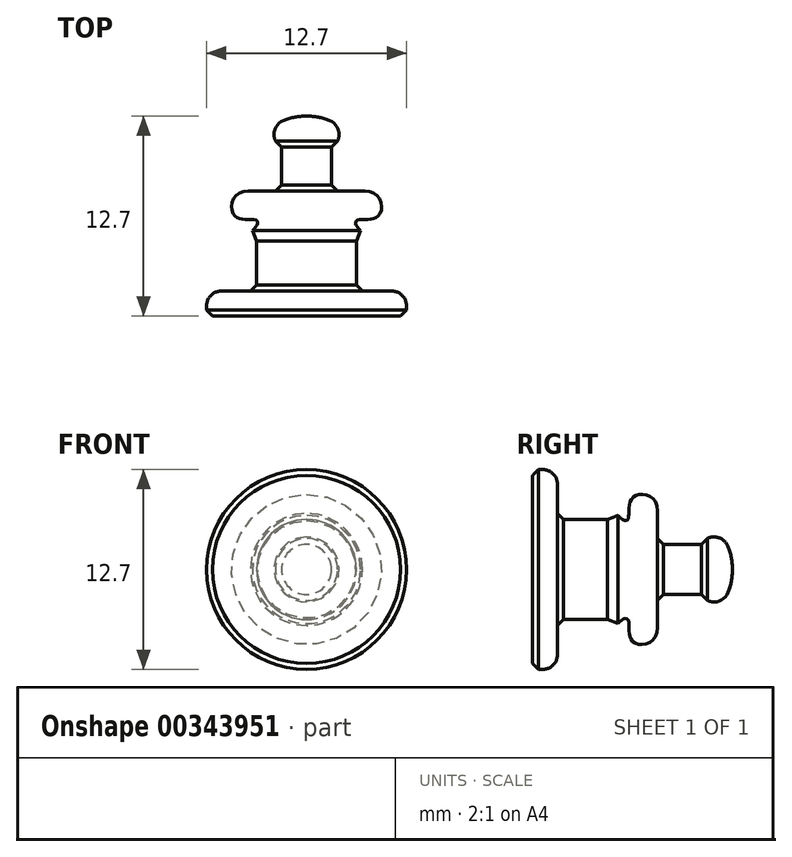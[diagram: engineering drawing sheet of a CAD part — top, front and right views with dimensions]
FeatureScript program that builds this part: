
annotation { "Feature Type Name" : "Feature", "Feature Type Description" : "" }
export const myFeature = defineFeature(function(context is Context, id is Id, definition is map)
    precondition{}
    {
        {
            var Q0;
            Q0=qCreatedBy(makeId("Right.planeOp"),FACE);
            var sketch = newSketch(context, id + "F0", { "sketchPlane" : qUnion([Q0])});
            skLineSegment(sketch, "E0", {"start": v(0, 0) * mm, "end": v(-12.7, 0) * mm});
            skLineSegment(sketch, "E1", {"start": v(-12.7, 0) * mm, "end": v(-12.7, 6.35) * mm});
            skLineSegment(sketch, "E2", {"start": v(-12.7, 6.35) * mm, "end": v(-11.11, 6.35) * mm});
            skLineSegment(sketch, "E3", {"start": v(-11.11, 6.35) * mm, "end": v(-11.11, 3.17) * mm});
            skLineSegment(sketch, "E4", {"start": v(-11.11, 3.17) * mm, "end": v(-7.94, 3.18) * mm});
            skLineSegment(sketch, "E5", {"start": v(-7.94, 3.18) * mm, "end": v(-7.94, 4.55) * mm});
            skFitSpline(sketch, "E6", {"points": [v(-7.94, 4.55) * mm, v(-6.64, 3.18) * mm, v(-6.35, 4.55) * mm, v(-4.76, 3.72) * mm], "startDerivative": vector(3.84, -9.69) * mm, "endDerivative": vector(0, -9.78) * mm});
            skArc(sketch, "E7", {"start": v(0, 0) * mm, "mid": v(-0.42, 1.77) * mm, "end": v(-1.59, 3.18) * mm});
            skLineSegment(sketch, "E8", {"start": v(-4.76, 1.59) * mm, "end": v(-1.59, 1.59) * mm});
            skLineSegment(sketch, "E9", {"start": v(-1.59, 1.59) * mm, "end": v(-1.59, 3.18) * mm});
            skLineSegment(sketch, "E10", {"start": v(-4.76, 1.59) * mm, "end": v(-4.76, 3.72) * mm});
            skSolve(sketch);
        }
        {
            var Q0;
            Q0=makeQuery(id+"F0.imprint","IMPRINT",FACE,{"disambiguationData":[TD([[makeQuery(id+"F0.imprint","IMPRINT",EDGE,{"derivedFrom":sQuery(id+"F0.wireOp",EDGE,"E0")}),-1.0]])]});
            var Q1;
            Q1=sQuery(id+"F0.wireOp",EDGE,"E0");
            revolve(context, id + "F1", {"entities" : qUnion([Q0]), "axis" : qUnion([Q1]), "revolveType" : RevolveType.FULL});
        }
        {
            var Q0;
            Q0=makeQuery(id+"F1.opRevolve","SWEPT_EDGE",EDGE,{"disambiguationData":[OSD([sQuery(id+"F0.wireOp",EDGE,"MyWxliaP-k4Tk-fx3N-ortE-LeMPfOSf4NQa"),sQuery(id+"F0.wireOp",EDGE,"E8")])]});
            var Q1;
            Q1=makeQuery(id+"F1.opRevolve","SWEPT_EDGE",EDGE,{"disambiguationData":[OSD([sQuery(id+"F0.wireOp",EDGE,"E5"),sQuery(id+"F0.wireOp",EDGE,"E6")])]});
            var Q2;
            {var subQ0=sQuery(id+"F0.wireOp",EDGE,"E9");Q2=makeQuery(id+"F3.opFillet","BLEND_EDGE",EDGE,{"blendedFrom":[makeQuery(id+"F1.opRevolve","SWEPT_EDGE",EDGE,{"disambiguationData":[OSD([sQuery(id+"F0.wireOp",EDGE,"E7"),subQ0])]}),makeQuery(id+"F1.opRevolve","SWEPT_FACE",FACE,{"disambiguationData":[OSD([subQ0])]})],"blendedInto":[makeQuery(id+"F1.opRevolve","SWEPT_FACE",FACE,{"disambiguationData":[OSD([subQ0])]})]});}
            var Q3;
            Q3=makeQuery(id+"F1.opRevolve","SWEPT_EDGE",EDGE,{"disambiguationData":[OSD([sQuery(id+"F0.wireOp",EDGE,"E1"),sQuery(id+"F0.wireOp",EDGE,"E2")])]});
            var Q4;
            Q4=makeQuery(id+"F1.opRevolve","SWEPT_EDGE",EDGE,{"disambiguationData":[OSD([sQuery(id+"F0.wireOp",EDGE,"E3"),sQuery(id+"F0.wireOp",EDGE,"E4")])]});
            chamfer(context, id + "F2", {"entities" : qUnion([Q0, Q1, Q2, Q3, Q4]), "width" : 0.38 * mm, "tangentPropagation" : true});
        }
        {
            var Q0;
            Q0=makeQuery(id+"F1.opRevolve","SWEPT_EDGE",EDGE,{"disambiguationData":[OSD([sQuery(id+"F0.wireOp",EDGE,"E7"),sQuery(id+"F0.wireOp",EDGE,"E9")])]});
            var Q1;
            Q1=makeQuery(id+"F1.opRevolve","SWEPT_EDGE",EDGE,{"disambiguationData":[OSD([sQuery(id+"F0.wireOp",EDGE,"E2"),sQuery(id+"F0.wireOp",EDGE,"E3")])]});
            var Q2;
            Q2=makeQuery(id+"F1.opRevolve","SWEPT_EDGE",EDGE,{"disambiguationData":[OSD([sQuery(id+"F0.wireOp",EDGE,"IASGdcMD-PzqD-RtkE-3gzn-0NcbffNXNx7e"),sQuery(id+"F0.wireOp",EDGE,"E6")])]});
            fillet(context, id + "F3", {"entities" : qUnion([Q0, Q1, Q2]), "radius" : 0.95 * mm, "tangentPropagation" : true, "allowEdgeOverflow" : false});
        }
    });
